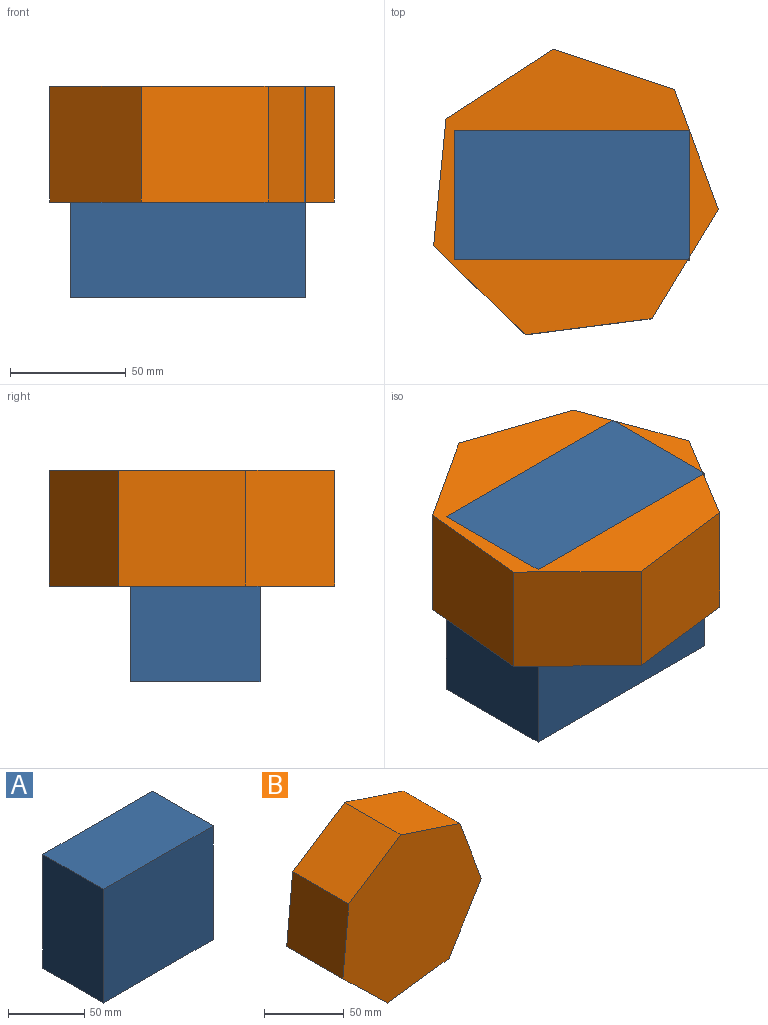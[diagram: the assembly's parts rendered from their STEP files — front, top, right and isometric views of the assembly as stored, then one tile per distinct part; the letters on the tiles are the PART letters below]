
ASSEMBLY  parts=2 mates=1
PART A: 6 faces, bbox 101.7x55.9x91.1 mm
  f0: plane 101.71x55.95mm, normal (0,0,1), area 5690.2mm2, adj f1,f3,f4,f5
  f1: plane 91.14x55.95mm, normal (-1,0,0), area 5099.1mm2, adj f0,f2,f4,f5
  f2: plane 101.71x55.95mm, normal (0,0,-1), area 5690.2mm2, adj f1,f3,f4,f5
  f3: plane 91.14x55.95mm, normal (1,0,0), area 5099.1mm2, adj f0,f2,f4,f5
  f4: plane 101.71x91.14mm, normal (0,-1,0), area 9270.3mm2, adj f0,f1,f2,f3
  f5: plane 101.71x91.14mm, normal (0,1,0), area 9270.3mm2, adj f0,f1,f2,f3
PART B: 9 faces, bbox 122.9x49.9x123.3 mm
  f0: plane 49.89x39.56mm, normal (-0.7,0,-0.72), area 2751mm2, adj f1,f6,f7,f8
  f1: plane 54.69x49.89mm, normal (0.13,0,-0.99), area 2751mm2, adj f0,f2,f7,f8
  f2: plane 49.89x47.12mm, normal (0.85,0,-0.52), area 2751mm2, adj f1,f3,f7,f8
  f3: plane 51.77x49.89mm, normal (0.94,0,0.34), area 2751mm2, adj f2,f4,f7,f8
  f4: plane 52.31x49.89mm, normal (0.32,0,0.95), area 2751mm2, adj f3,f5,f7,f8
  f5: plane 49.89x46.25mm, normal (-0.54,0,0.84), area 2751mm2, adj f4,f6,f7,f8
  f6: plane 54.88x49.89mm, normal (-1,0,0.1), area 2751mm2, adj f0,f5,f7,f8
  f7: plane 123.31x122.9mm, normal (0,1,0), area 11048mm2, adj f0,f1,f2,f3,f4,f5,f6
  f8: plane 123.31x122.9mm, normal (0,-1,0), area 11048mm2, adj f0,f1,f2,f3,f4,f5,f6
PLACE A at identity
PLACE B rot(axis=(-1,0,0),90deg) t=(-23.93,-47.65,44.12)mm
MATE fastened B.f8 <-> A.f0  axis (0,0,1) through (4.45,-27.97,44.12)mm
